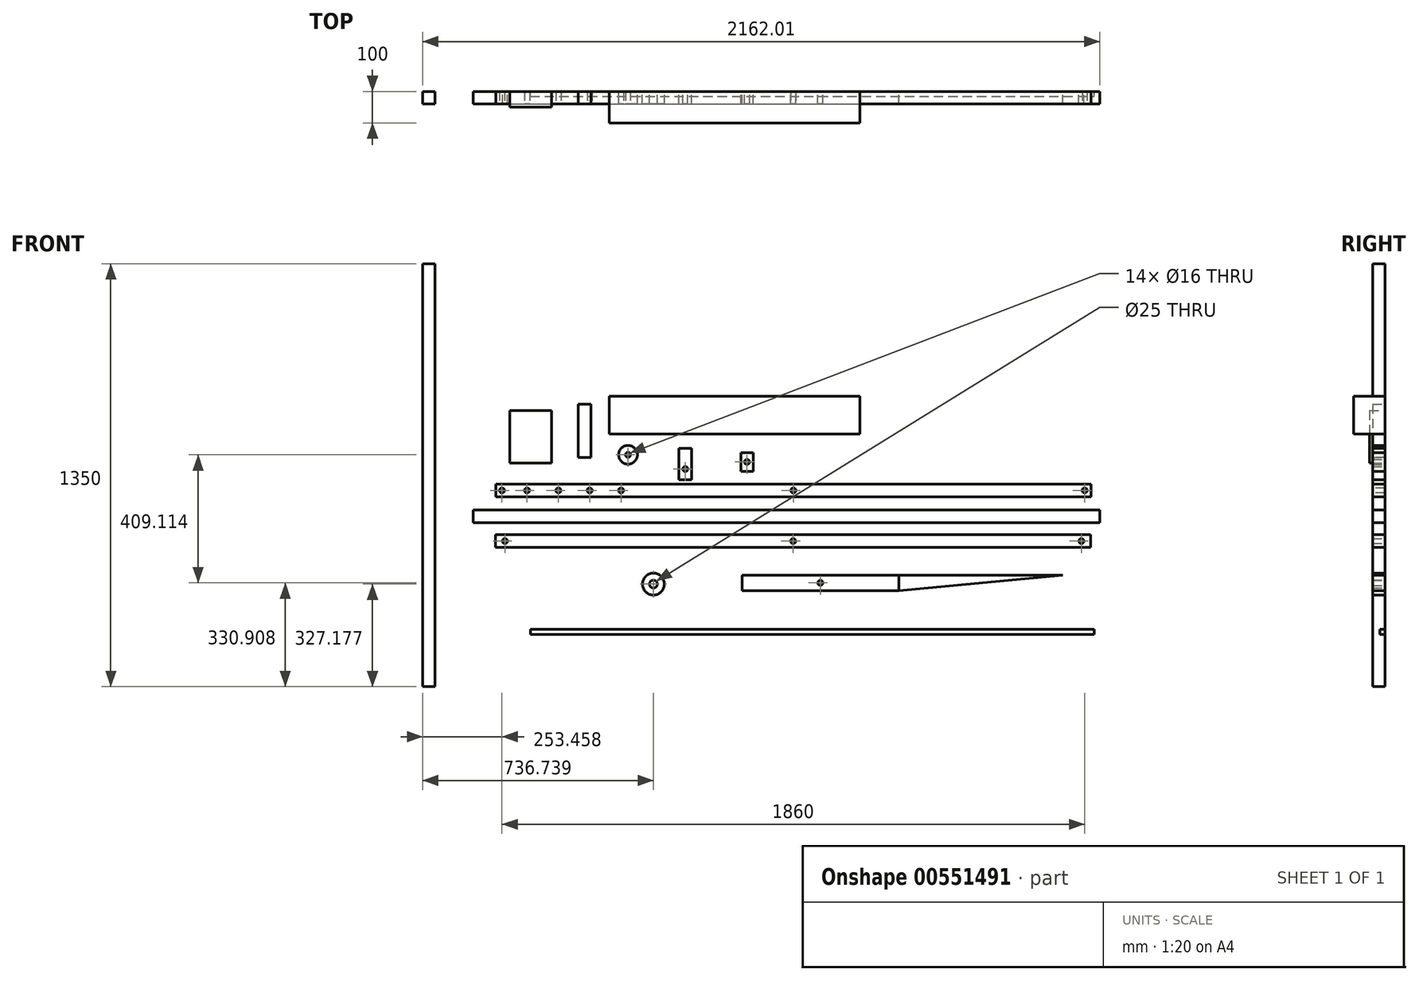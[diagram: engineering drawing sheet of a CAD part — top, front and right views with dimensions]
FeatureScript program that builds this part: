
annotation { "Feature Type Name" : "Feature", "Feature Type Description" : "" }
export const myFeature = defineFeature(function(context is Context, id is Id, definition is map)
    precondition{}
    {
        {
            var Q0;
            Q0=qCreatedBy(makeId("Front.planeOp"),FACE);
            var sketch = newSketch(context, id + "F0", { "sketchPlane" : qUnion([Q0])});
            skLineSegment(sketch, "E0.bottom", {"start": v(-551.41, 0) * mm, "end": v(1348.59, 0) * mm});
            skLineSegment(sketch, "E0.top", {"start": v(-551.41, 40) * mm, "end": v(1348.59, 40) * mm});
            skLineSegment(sketch, "E0.left", {"start": v(-551.41, 0) * mm, "end": v(-551.41, 40) * mm});
            skLineSegment(sketch, "E0.right", {"start": v(1348.59, 0) * mm, "end": v(1348.59, 40) * mm});
            skSolve(sketch);
        }
        {
            var Q0;
            Q0=makeQuery(id+"F0.imprint","IMPRINT",FACE,{"disambiguationData":[TD([[makeQuery(id+"F0.imprint","IMPRINT",EDGE,{"derivedFrom":sQuery(id+"F0.wireOp",EDGE,"E0.bottom")}),1.0]])]});
            extrude(context, id + "F1", {"entities" : qUnion([Q0]), "depth" : 40 * mm, "offsetDistance" : 25 * mm});
        }
        {
            var Q0;
            Q0=makeQuery(id+"F1.opExtrude","CAP_FACE",FACE,{"disambiguationData":[OSD([sQuery(id+"F0.wireOp",EDGE,"E0.bottom"),sQuery(id+"F0.wireOp",EDGE,"E0.top"),sQuery(id+"F0.wireOp",EDGE,"E0.left"),sQuery(id+"F0.wireOp",EDGE,"E0.right")])],"isStart":false});
            var sketch = newSketch(context, id + "F2", { "sketchPlane" : qUnion([Q0])});
            skCircle(sketch, "E1", {"center": v(1328.59, 20) * mm, "radius": 8 * mm});
            skPoint(sketch, "E1.centerSnap0", {"position": v(1348.59, 20) * mm});
            skCircle(sketch, "E2", {"center": v(398.59, 20) * mm, "radius": 8 * mm});
            skPoint(sketch, "E2.centerSnap0", {"position": v(398.59, 40) * mm});
            skPoint(sketch, "E2.centerSnap1", {"position": v(-551.41, 20) * mm});
            skCircle(sketch, "E3", {"center": v(-531.41, 20) * mm, "radius": 8 * mm});
            skSolve(sketch);
        }
        {
            var Q0;
            Q0=makeQuery(id+"F2.imprint","IMPRINT",FACE,{"disambiguationData":[TD([[makeQuery(id+"F2.imprint","IMPRINT",EDGE,{"derivedFrom":sQuery(id+"F2.wireOp",EDGE,"E3")}),1.0]])]});
            extrude(context, id + "F3", {"entities" : qUnion([Q0]), "operationType" : NewBodyOperationType.REMOVE, "oppositeDirection" : true, "depth" : 40 * mm, "offsetDistance" : 25 * mm});
        }
        {
            var Q0;
            Q0=makeQuery(id+"F1.opExtrude","CAP_FACE",FACE,{"disambiguationData":[OSD([sQuery(id+"F0.wireOp",EDGE,"E0.bottom"),sQuery(id+"F0.wireOp",EDGE,"E0.top"),sQuery(id+"F0.wireOp",EDGE,"E0.left"),sQuery(id+"F0.wireOp",EDGE,"E0.right")])],"isStart":false});
            var sketch = newSketch(context, id + "F4", { "sketchPlane" : qUnion([Q0])});
            skCircle(sketch, "E4", {"center": v(398.59, 20) * mm, "radius": 8 * mm});
            skPoint(sketch, "E4.centerSnap0", {"position": v(-551.41, 20) * mm});
            skPoint(sketch, "E4.centerSnap1", {"position": v(398.59, 0) * mm});
            skSolve(sketch);
        }
        {
            var Q0;
            Q0=makeQuery(id+"F4.imprint","IMPRINT",FACE,{"disambiguationData":[TD([[makeQuery(id+"F4.imprint","IMPRINT",EDGE,{"derivedFrom":sQuery(id+"F4.wireOp",EDGE,"E4")}),1.0]])]});
            extrude(context, id + "F5", {"entities" : qUnion([Q0]), "operationType" : NewBodyOperationType.REMOVE, "oppositeDirection" : true, "depth" : 40 * mm, "offsetDistance" : 25 * mm});
        }
        {
            var Q0;
            Q0=makeQuery(id+"F1.opExtrude","CAP_FACE",FACE,{"disambiguationData":[OSD([sQuery(id+"F0.wireOp",EDGE,"E0.bottom"),sQuery(id+"F0.wireOp",EDGE,"E0.top"),sQuery(id+"F0.wireOp",EDGE,"E0.left"),sQuery(id+"F0.wireOp",EDGE,"E0.right")])],"isStart":false});
            var sketch = newSketch(context, id + "F6", { "sketchPlane" : qUnion([Q0])});
            skCircle(sketch, "E5", {"center": v(1328.59, 20) * mm, "radius": 8 * mm});
            skPoint(sketch, "E5.centerSnap0", {"position": v(1348.59, 20) * mm});
            skSolve(sketch);
        }
        {
            var Q0;
            Q0=makeQuery(id+"F6.imprint","IMPRINT",FACE,{"disambiguationData":[TD([[makeQuery(id+"F6.imprint","IMPRINT",EDGE,{"derivedFrom":sQuery(id+"F6.wireOp",EDGE,"E5")}),1.0]])]});
            extrude(context, id + "F7", {"entities" : qUnion([Q0]), "operationType" : NewBodyOperationType.REMOVE, "oppositeDirection" : true, "depth" : 40 * mm, "offsetDistance" : 25 * mm});
        }
        {
            var Q0;
            Q0=qCreatedBy(makeId("Front.planeOp"),FACE);
            var sketch = newSketch(context, id + "F8", { "sketchPlane" : qUnion([Q0])});
            skCircle(sketch, "E6", {"center": v(-129.26, 134) * mm, "radius": 30 * mm});
            skSolve(sketch);
        }
        {
            var Q0;
            Q0=makeQuery(id+"F8.imprint","IMPRINT",FACE,{"disambiguationData":[TD([[makeQuery(id+"F8.imprint","IMPRINT",EDGE,{"derivedFrom":sQuery(id+"F8.wireOp",EDGE,"E6")}),1.0]])]});
            extrude(context, id + "F9", {"entities" : qUnion([Q0]), "depth" : 40 * mm, "offsetDistance" : 25 * mm});
        }
        {
            var Q0;
            Q0=makeQuery(id+"F9.opExtrude","CAP_FACE",FACE,{"disambiguationData":[OSD([sQuery(id+"F8.wireOp",EDGE,"E6")])],"isStart":false});
            var sketch = newSketch(context, id + "F10", { "sketchPlane" : qUnion([Q0])});
            skCircle(sketch, "E7", {"center": v(-129.26, 134) * mm, "radius": 8 * mm});
            skSolve(sketch);
        }
        {
            var Q0;
            Q0=makeQuery(id+"F10.imprint","IMPRINT",FACE,{"disambiguationData":[TD([[makeQuery(id+"F10.imprint","IMPRINT",EDGE,{"derivedFrom":sQuery(id+"F10.wireOp",EDGE,"E7")}),1.0]])]});
            extrude(context, id + "F11", {"entities" : qUnion([Q0]), "operationType" : NewBodyOperationType.REMOVE, "oppositeDirection" : true, "depth" : 40 * mm, "offsetDistance" : 25 * mm});
        }
        {
            var Q0;
            Q0=qCreatedBy(makeId("Front.planeOp"),FACE);
            var sketch = newSketch(context, id + "F12", { "sketchPlane" : qUnion([Q0])});
            skLineSegment(sketch, "E8.bottom", {"start": v(230.76, 81.04) * mm, "end": v(270.76, 81.04) * mm});
            skLineSegment(sketch, "E8.top", {"start": v(230.76, 141.04) * mm, "end": v(270.76, 141.04) * mm});
            skLineSegment(sketch, "E8.left", {"start": v(230.76, 81.04) * mm, "end": v(230.76, 141.04) * mm});
            skLineSegment(sketch, "E8.right", {"start": v(270.76, 81.04) * mm, "end": v(270.76, 141.04) * mm});
            skPoint(sketch, "E9.centerSnap0", {"position": v(250.76, 141.04) * mm});
            skPoint(sketch, "E9.centerSnap1", {"position": v(230.76, 111.04) * mm});
            skCircle(sketch, "E10", {"center": v(250.76, 111.04) * mm, "radius": 8 * mm});
            skSolve(sketch);
        }
        {
            var Q0;
            Q0=makeQuery(id+"F12.imprint","IMPRINT",FACE,{"disambiguationData":[TD([[makeQuery(id+"F12.imprint","IMPRINT",EDGE,{"derivedFrom":sQuery(id+"F12.wireOp",EDGE,"E8.bottom")}),1.0]])]});
            extrude(context, id + "F13", {"entities" : qUnion([Q0]), "depth" : 40 * mm, "offsetDistance" : 25 * mm});
        }
        {
            var Q0;
            Q0=qCreatedBy(makeId("Front.planeOp"),FACE);
            var sketch = newSketch(context, id + "F14", { "sketchPlane" : qUnion([Q0])});
            skLineSegment(sketch, "E11.bottom", {"start": v(-622.86, -42.73) * mm, "end": v(1377.14, -42.73) * mm});
            skLineSegment(sketch, "E11.top", {"start": v(-622.86, -82.73) * mm, "end": v(1377.14, -82.73) * mm});
            skLineSegment(sketch, "E11.left", {"start": v(-622.86, -42.73) * mm, "end": v(-622.86, -82.73) * mm});
            skLineSegment(sketch, "E11.right", {"start": v(1377.14, -42.73) * mm, "end": v(1377.14, -82.73) * mm});
            skSolve(sketch);
        }
        {
            var Q0;
            Q0=makeQuery(id+"F14.imprint","IMPRINT",FACE,{"disambiguationData":[TD([[makeQuery(id+"F14.imprint","IMPRINT",EDGE,{"derivedFrom":sQuery(id+"F14.wireOp",EDGE,"E11.bottom")}),-1.0]])]});
            extrude(context, id + "F15", {"entities" : qUnion([Q0]), "depth" : 40 * mm, "offsetDistance" : 25 * mm});
        }
        {
            var Q0;
            Q0=qCreatedBy(makeId("Front.planeOp"),FACE);
            var sketch = newSketch(context, id + "F16", { "sketchPlane" : qUnion([Q0])});
            skLineSegment(sketch, "E12.bottom", {"start": v(-189.5, 320.9) * mm, "end": v(610.5, 320.9) * mm});
            skLineSegment(sketch, "E12.top", {"start": v(-189.5, 200.9) * mm, "end": v(610.5, 200.9) * mm});
            skLineSegment(sketch, "E12.left", {"start": v(-189.5, 320.9) * mm, "end": v(-189.5, 200.9) * mm});
            skLineSegment(sketch, "E12.right", {"start": v(610.5, 320.9) * mm, "end": v(610.5, 200.9) * mm});
            skSolve(sketch);
        }
        {
            var Q0;
            Q0=makeQuery(id+"F16.imprint","IMPRINT",FACE,{"disambiguationData":[TD([[makeQuery(id+"F16.imprint","IMPRINT",EDGE,{"derivedFrom":sQuery(id+"F16.wireOp",EDGE,"E12.bottom")}),-1.0]])]});
            extrude(context, id + "F17", {"entities" : qUnion([Q0]), "depth" : 100 * mm, "offsetDistance" : 25 * mm});
        }
        {
            var Q0;
            Q0=makeQuery(id+"F1.opExtrude","CAP_FACE",FACE,{"disambiguationData":[OSD([sQuery(id+"F0.wireOp",EDGE,"E0.bottom"),sQuery(id+"F0.wireOp",EDGE,"E0.top"),sQuery(id+"F0.wireOp",EDGE,"E0.left"),sQuery(id+"F0.wireOp",EDGE,"E0.right")])],"isStart":false});
            var sketch = newSketch(context, id + "F18", { "sketchPlane" : qUnion([Q0])});
            skCircle(sketch, "E13", {"center": v(-451.41, 20) * mm, "radius": 8 * mm});
            skPoint(sketch, "E13.centerSnap0", {"position": v(-551.41, 20) * mm});
            skSolve(sketch);
        }
        {
            var Q0;
            Q0=makeQuery(id+"F18.imprint","IMPRINT",FACE,{"disambiguationData":[TD([[makeQuery(id+"F18.imprint","IMPRINT",EDGE,{"derivedFrom":sQuery(id+"F18.wireOp",EDGE,"E13")}),1.0]])]});
            extrude(context, id + "F19", {"entities" : qUnion([Q0]), "operationType" : NewBodyOperationType.REMOVE, "oppositeDirection" : true, "depth" : 40 * mm, "offsetDistance" : 25 * mm});
        }
        {
            var Q0;
            Q0=makeQuery(id+"F1.opExtrude","CAP_FACE",FACE,{"disambiguationData":[OSD([sQuery(id+"F0.wireOp",EDGE,"E0.bottom"),sQuery(id+"F0.wireOp",EDGE,"E0.top"),sQuery(id+"F0.wireOp",EDGE,"E0.left"),sQuery(id+"F0.wireOp",EDGE,"E0.right")])],"isStart":false});
            var sketch = newSketch(context, id + "F20", { "sketchPlane" : qUnion([Q0])});
            skCircle(sketch, "E14", {"center": v(-351.41, 20) * mm, "radius": 8 * mm});
            skPoint(sketch, "E14.centerSnap0", {"position": v(-551.41, 20) * mm});
            skSolve(sketch);
        }
        {
            var Q0;
            Q0=makeQuery(id+"F20.imprint","IMPRINT",FACE,{"disambiguationData":[TD([[makeQuery(id+"F20.imprint","IMPRINT",EDGE,{"derivedFrom":sQuery(id+"F20.wireOp",EDGE,"E14")}),1.0]])]});
            extrude(context, id + "F21", {"entities" : qUnion([Q0]), "operationType" : NewBodyOperationType.REMOVE, "oppositeDirection" : true, "depth" : 40 * mm, "offsetDistance" : 25 * mm});
        }
        {
            var Q0;
            Q0=qCreatedBy(makeId("Front.planeOp"),FACE);
            var sketch = newSketch(context, id + "F22", { "sketchPlane" : qUnion([Q0])});
            skLineSegment(sketch, "E15.bottom", {"start": v(33.68, 154.26) * mm, "end": v(73.68, 154.26) * mm});
            skLineSegment(sketch, "E15.top", {"start": v(33.68, 54.26) * mm, "end": v(73.68, 54.26) * mm});
            skLineSegment(sketch, "E15.left", {"start": v(33.68, 154.26) * mm, "end": v(33.68, 54.26) * mm});
            skLineSegment(sketch, "E15.right", {"start": v(73.68, 154.26) * mm, "end": v(73.68, 54.26) * mm});
            skCircle(sketch, "E16", {"center": v(53.68, 88.45) * mm, "radius": 8 * mm});
            skPoint(sketch, "E16.centerSnap0", {"position": v(53.68, 54.26) * mm});
            skSolve(sketch);
        }
        {
            var Q0;
            Q0=makeQuery(id+"F22.imprint","IMPRINT",FACE,{"disambiguationData":[TD([[makeQuery(id+"F22.imprint","IMPRINT",EDGE,{"derivedFrom":sQuery(id+"F22.wireOp",EDGE,"E15.bottom")}),-1.0]])]});
            extrude(context, id + "F23", {"entities" : qUnion([Q0]), "depth" : 40 * mm, "offsetDistance" : 25 * mm});
        }
        {
            var Q0;
            Q0=qCreatedBy(makeId("Front.planeOp"),FACE);
            var sketch = newSketch(context, id + "F24", { "sketchPlane" : qUnion([Q0])});
            skLineSegment(sketch, "E17.bottom", {"start": v(-506.17, 275.09) * mm, "end": v(-373.67, 275.09) * mm});
            skLineSegment(sketch, "E17.top", {"start": v(-506.17, 106.97) * mm, "end": v(-373.67, 106.97) * mm});
            skLineSegment(sketch, "E17.left", {"start": v(-506.17, 275.09) * mm, "end": v(-506.17, 106.97) * mm});
            skLineSegment(sketch, "E17.right", {"start": v(-373.67, 275.09) * mm, "end": v(-373.67, 106.97) * mm});
            skSolve(sketch);
        }
        {
            var Q0;
            Q0=makeQuery(id+"F24.imprint","IMPRINT",FACE,{"disambiguationData":[TD([[makeQuery(id+"F24.imprint","IMPRINT",EDGE,{"derivedFrom":sQuery(id+"F24.wireOp",EDGE,"E17.bottom")}),-1.0]])]});
            extrude(context, id + "F25", {"entities" : qUnion([Q0]), "depth" : 50 * mm, "offsetDistance" : 25 * mm});
        }
        {
            var Q0;
            Q0=makeQuery(id+"F1.opExtrude","CAP_FACE",FACE,{"disambiguationData":[OSD([sQuery(id+"F0.wireOp",EDGE,"E0.bottom"),sQuery(id+"F0.wireOp",EDGE,"E0.top"),sQuery(id+"F0.wireOp",EDGE,"E0.left"),sQuery(id+"F0.wireOp",EDGE,"E0.right")])],"isStart":false});
            var sketch = newSketch(context, id + "F26", { "sketchPlane" : qUnion([Q0])});
            skCircle(sketch, "E18", {"center": v(-264.69, 20) * mm, "radius": 8 * mm});
            skPoint(sketch, "E18.centerSnap0", {"position": v(-551.41, 20) * mm});
            skCircle(sketch, "E19", {"center": v(-162.1, 20) * mm, "radius": 8 * mm});
            skSolve(sketch);
        }
        {
            var Q0;
            Q0=makeQuery(id+"F26.imprint","IMPRINT",FACE,{"disambiguationData":[TD([[makeQuery(id+"F26.imprint","IMPRINT",EDGE,{"derivedFrom":sQuery(id+"F26.wireOp",EDGE,"E18")}),1.0]])]});
            extrude(context, id + "F27", {"entities" : qUnion([Q0]), "operationType" : NewBodyOperationType.REMOVE, "oppositeDirection" : true, "depth" : -40 * mm, "offsetDistance" : 25 * mm});
        }
        {
            var Q0;
            Q0=makeQuery(id+"F1.opExtrude","CAP_FACE",FACE,{"disambiguationData":[OSD([sQuery(id+"F0.wireOp",EDGE,"E0.bottom"),sQuery(id+"F0.wireOp",EDGE,"E0.top"),sQuery(id+"F0.wireOp",EDGE,"E0.left"),sQuery(id+"F0.wireOp",EDGE,"E0.right")])],"isStart":false});
            var sketch = newSketch(context, id + "F28", { "sketchPlane" : qUnion([Q0])});
            skCircle(sketch, "E20", {"center": v(-251.41, 20) * mm, "radius": 8 * mm});
            skPoint(sketch, "E20.centerSnap0", {"position": v(-551.41, 20) * mm});
            skCircle(sketch, "E21", {"center": v(-151.41, 20) * mm, "radius": 8 * mm});
            skSolve(sketch);
        }
        {
            var Q0;
            Q0=makeQuery(id+"F28.imprint","IMPRINT",FACE,{"disambiguationData":[TD([[makeQuery(id+"F28.imprint","IMPRINT",EDGE,{"derivedFrom":sQuery(id+"F28.wireOp",EDGE,"E20")}),1.0]])]});
            extrude(context, id + "F29", {"entities" : qUnion([Q0]), "operationType" : NewBodyOperationType.REMOVE, "oppositeDirection" : true, "depth" : 40 * mm, "offsetDistance" : 25 * mm});
        }
        {
            var Q0;
            Q0=makeQuery(id+"F1.opExtrude","CAP_FACE",FACE,{"disambiguationData":[OSD([sQuery(id+"F0.wireOp",EDGE,"E0.bottom"),sQuery(id+"F0.wireOp",EDGE,"E0.top"),sQuery(id+"F0.wireOp",EDGE,"E0.left"),sQuery(id+"F0.wireOp",EDGE,"E0.right")])],"isStart":false});
            var sketch = newSketch(context, id + "F30", { "sketchPlane" : qUnion([Q0])});
            skCircle(sketch, "E22", {"center": v(-151.41, 20) * mm, "radius": 8 * mm});
            skPoint(sketch, "E22.centerSnap0", {"position": v(-551.41, 20) * mm});
            skSolve(sketch);
        }
        {
            var Q0;
            Q0=makeQuery(id+"F30.imprint","IMPRINT",FACE,{"disambiguationData":[TD([[makeQuery(id+"F30.imprint","IMPRINT",EDGE,{"derivedFrom":sQuery(id+"F30.wireOp",EDGE,"E22")}),1.0]])]});
            extrude(context, id + "F31", {"entities" : qUnion([Q0]), "operationType" : NewBodyOperationType.REMOVE, "oppositeDirection" : true, "depth" : 40 * mm, "offsetDistance" : 25 * mm});
        }
        {
            var Q0;
            Q0=qCreatedBy(makeId("Front.planeOp"),FACE);
            var sketch = newSketch(context, id + "F32", { "sketchPlane" : qUnion([Q0])});
            skLineSegment(sketch, "E23.bottom", {"start": v(-551.93, -121.58) * mm, "end": v(1348.07, -121.58) * mm});
            skLineSegment(sketch, "E23.top", {"start": v(-551.93, -161.58) * mm, "end": v(1348.07, -161.58) * mm});
            skLineSegment(sketch, "E23.left", {"start": v(-551.93, -121.58) * mm, "end": v(-551.93, -161.58) * mm});
            skLineSegment(sketch, "E23.right", {"start": v(1348.07, -121.58) * mm, "end": v(1348.07, -161.58) * mm});
            skCircle(sketch, "E24", {"center": v(398.07, -141.58) * mm, "radius": 8 * mm});
            skPoint(sketch, "E24.centerSnap0", {"position": v(398.07, -121.58) * mm});
            skPoint(sketch, "E24.centerSnap1", {"position": v(-551.93, -141.58) * mm});
            skCircle(sketch, "E25", {"center": v(-521.93, -141.58) * mm, "radius": 8 * mm});
            skCircle(sketch, "E26", {"center": v(1318.07, -141.58) * mm, "radius": 8 * mm});
            skPoint(sketch, "E26.centerSnap0", {"position": v(1348.07, -141.58) * mm});
            skSolve(sketch);
        }
        {
            var Q0;
            Q0=makeQuery(id+"F32.imprint","IMPRINT",FACE,{"disambiguationData":[TD([[makeQuery(id+"F32.imprint","IMPRINT",EDGE,{"derivedFrom":sQuery(id+"F32.wireOp",EDGE,"E23.bottom")}),-1.0]])]});
            extrude(context, id + "F33", {"entities" : qUnion([Q0]), "depth" : 40 * mm, "offsetDistance" : 25 * mm});
        }
        {
            var Q0;
            Q0=qCreatedBy(makeId("Front.planeOp"),FACE);
            var sketch = newSketch(context, id + "F34", { "sketchPlane" : qUnion([Q0])});
            skLineSegment(sketch, "E27.bottom", {"start": v(-287.62, 295.08) * mm, "end": v(-247.62, 295.08) * mm});
            skLineSegment(sketch, "E27.top", {"start": v(-287.62, 125.08) * mm, "end": v(-247.62, 125.08) * mm});
            skLineSegment(sketch, "E27.left", {"start": v(-287.62, 295.08) * mm, "end": v(-287.62, 125.08) * mm});
            skLineSegment(sketch, "E27.right", {"start": v(-247.62, 295.08) * mm, "end": v(-247.62, 125.08) * mm});
            skSolve(sketch);
        }
        {
            var Q0;
            Q0=makeQuery(id+"F34.imprint","IMPRINT",FACE,{"disambiguationData":[TD([[makeQuery(id+"F34.imprint","IMPRINT",EDGE,{"derivedFrom":sQuery(id+"F34.wireOp",EDGE,"E27.bottom")}),-1.0]])]});
            extrude(context, id + "F35", {"entities" : qUnion([Q0]), "depth" : 40 * mm, "offsetDistance" : 25 * mm});
        }
        {
            var Q0;
            Q0=qCreatedBy(makeId("Front.planeOp"),FACE);
            var sketch = newSketch(context, id + "F36", { "sketchPlane" : qUnion([Q0])});
            skLineSegment(sketch, "E28.bottom", {"start": v(234.8, -250.12) * mm, "end": v(734.8, -250.12) * mm});
            skLineSegment(sketch, "E28.top", {"start": v(234.8, -300.12) * mm, "end": v(734.8, -300.12) * mm});
            skLineSegment(sketch, "E28.left", {"start": v(234.8, -250.12) * mm, "end": v(234.8, -300.12) * mm});
            skLineSegment(sketch, "E28.right", {"start": v(734.8, -250.12) * mm, "end": v(734.8, -300.12) * mm});
            skCircle(sketch, "E29", {"center": v(484.8, -275.12) * mm, "radius": 8 * mm});
            skPoint(sketch, "E29.centerSnap0", {"position": v(484.8, -250.12) * mm});
            skPoint(sketch, "E29.centerSnap1", {"position": v(234.8, -275.12) * mm});
            skSolve(sketch);
        }
        {
            var Q0;
            Q0=makeQuery(id+"F36.imprint","IMPRINT",FACE,{"disambiguationData":[TD([[makeQuery(id+"F36.imprint","IMPRINT",EDGE,{"derivedFrom":sQuery(id+"F36.wireOp",EDGE,"E28.bottom")}),-1.0]])]});
            var sketch = newSketch(context, id + "F37", { "sketchPlane" : qUnion([Q0])});
            skPoint(sketch, "E30.0", {"position": v(734.8, -250.12) * mm});
            skLineSegment(sketch, "E31", {"start": v(734.8, -250.12) * mm, "end": v(1258.3, -250.12) * mm});
            skLineSegment(sketch, "E32", {"start": v(1258.3, -250.12) * mm, "end": v(734.8, -300.18) * mm});
            skLineSegment(sketch, "E33", {"start": v(734.8, -300.18) * mm, "end": v(734.8, -250.12) * mm});
            skSolve(sketch);
        }
        {
            var Q0;
            Q0=makeQuery(id+"F36.imprint","IMPRINT",FACE,{"disambiguationData":[TD([[makeQuery(id+"F36.imprint","IMPRINT",EDGE,{"derivedFrom":sQuery(id+"F36.wireOp",EDGE,"E28.bottom")}),-1.0]])]});
            var Q1;
            {var subQ0=sQuery(id+"F37.wireOp",EDGE,"E31");Q1=makeQuery(id+"F37.imprint","IMPRINT",FACE,{"disambiguationData":[TD([[makeQuery(id+"F37.imprint","IMPRINT",EDGE,{"derivedFrom":subQ0}),-1.0]])]});}
            extrude(context, id + "F38", {"entities" : qUnion([Q0, Q1]), "depth" : 40 * mm, "offsetDistance" : 25 * mm});
        }
        {
            var Q0;
            Q0=qCreatedBy(makeId("Front.planeOp"),FACE);
            var sketch = newSketch(context, id + "F39", { "sketchPlane" : qUnion([Q0])});
            skCircle(sketch, "E34", {"center": v(-48.13, -278.85) * mm, "radius": 12.5 * mm});
            skCircle(sketch, "E35", {"center": v(-48.13, -278.85) * mm, "radius": 35 * mm});
            skSolve(sketch);
        }
        {
            var Q0;
            Q0=makeQuery(id+"F39.imprint","IMPRINT",FACE,{"disambiguationData":[TD([[makeQuery(id+"F39.imprint","IMPRINT",EDGE,{"derivedFrom":sQuery(id+"F39.wireOp",EDGE,"E34")}),-1.0]])]});
            extrude(context, id + "F40", {"entities" : qUnion([Q0]), "depth" : 40 * mm, "offsetDistance" : 25 * mm});
        }
        {
            var Q0;
            Q0=qCreatedBy(makeId("Front.planeOp"),FACE);
            var sketch = newSketch(context, id + "F41", { "sketchPlane" : qUnion([Q0])});
            skLineSegment(sketch, "E36.bottom", {"start": v(-784.87, 743.97) * mm, "end": v(-744.87, 743.97) * mm});
            skLineSegment(sketch, "E36.top", {"start": v(-784.87, -606.03) * mm, "end": v(-744.87, -606.03) * mm});
            skLineSegment(sketch, "E36.left", {"start": v(-784.87, 743.97) * mm, "end": v(-784.87, -606.03) * mm});
            skLineSegment(sketch, "E36.right", {"start": v(-744.87, 743.97) * mm, "end": v(-744.87, -606.03) * mm});
            skSolve(sketch);
        }
        {
            var Q0;
            Q0=makeQuery(id+"F41.imprint","IMPRINT",FACE,{"disambiguationData":[TD([[makeQuery(id+"F41.imprint","IMPRINT",EDGE,{"derivedFrom":sQuery(id+"F41.wireOp",EDGE,"E36.bottom")}),-1.0]])]});
            extrude(context, id + "F42", {"entities" : qUnion([Q0]), "depth" : 40 * mm, "offsetDistance" : 25 * mm});
        }
        {
            var Q0;
            Q0=qCreatedBy(makeId("Front.planeOp"),FACE);
            var sketch = newSketch(context, id + "F43", { "sketchPlane" : qUnion([Q0])});
            skLineSegment(sketch, "E37.bottom", {"start": v(-441.15, -423.25) * mm, "end": v(1358.85, -423.25) * mm});
            skLineSegment(sketch, "E37.top", {"start": v(-441.15, -439.25) * mm, "end": v(1358.85, -439.25) * mm});
            skLineSegment(sketch, "E37.left", {"start": v(-441.15, -423.25) * mm, "end": v(-441.15, -439.25) * mm});
            skLineSegment(sketch, "E37.right", {"start": v(1358.85, -423.25) * mm, "end": v(1358.85, -439.25) * mm});
            skSolve(sketch);
        }
        {
            var Q0;
            Q0 = qSketchRegion(id + "F43", true);
            extrude(context, id + "F44", {"entities" : qUnion([Q0]), "depth" : 16 * mm, "offsetDistance" : 25 * mm});
        }
    });
